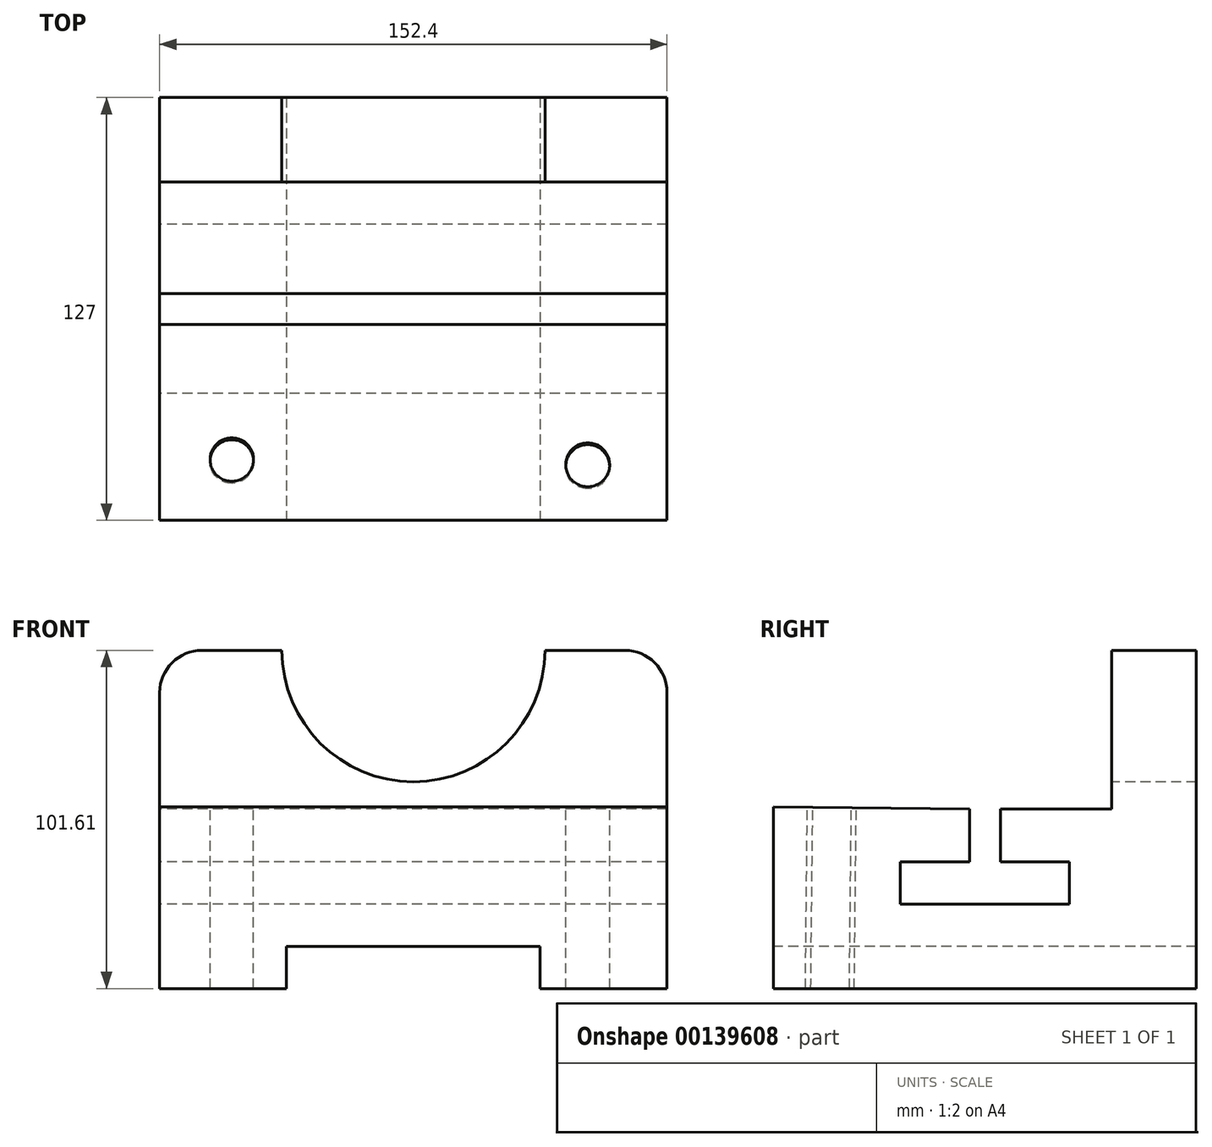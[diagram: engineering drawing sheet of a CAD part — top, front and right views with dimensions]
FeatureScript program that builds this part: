
annotation { "Feature Type Name" : "Feature", "Feature Type Description" : "" }
export const myFeature = defineFeature(function(context is Context, id is Id, definition is map)
    precondition{}
    {
        {
            var Q0;
            Q0=qCreatedBy(makeId("Right.planeOp"),FACE);
            var sketch = newSketch(context, id + "F0", { "sketchPlane" : qUnion([Q0])});
            skLineSegment(sketch, "E0", {"start": v(42.75, 47.63) * mm, "end": v(42.75, 0) * mm});
            skLineSegment(sketch, "E1", {"start": v(42.75, 0) * mm, "end": v(9.3, 0) * mm});
            skLineSegment(sketch, "E2", {"start": v(9.3, 0) * mm, "end": v(9.3, -15.87) * mm});
            skLineSegment(sketch, "E3", {"start": v(9.3, -15.87) * mm, "end": v(30.05, -15.87) * mm});
            skLineSegment(sketch, "E4", {"start": v(30.05, -15.87) * mm, "end": v(30.05, -28.57) * mm});
            skLineSegment(sketch, "E5", {"start": v(30.05, -28.57) * mm, "end": v(-20.75, -28.58) * mm});
            skLineSegment(sketch, "E6", {"start": v(-20.75, -28.58) * mm, "end": v(-20.75, -15.88) * mm});
            skLineSegment(sketch, "E7", {"start": v(-20.75, -15.88) * mm, "end": v(0, -15.88) * mm});
            skLineSegment(sketch, "E8", {"start": v(0, -15.88) * mm, "end": v(0, 0) * mm});
            skLineSegment(sketch, "E9", {"start": v(42.75, 47.63) * mm, "end": v(68.15, 47.63) * mm});
            skLineSegment(sketch, "E10", {"start": v(68.15, 47.63) * mm, "end": v(68.15, -53.97) * mm});
            skLineSegment(sketch, "E11", {"start": v(68.15, -53.97) * mm, "end": v(-58.85, -53.98) * mm});
            skLineSegment(sketch, "E12", {"start": v(-58.85, -53.98) * mm, "end": v(-58.85, 0.64) * mm});
            skLineSegment(sketch, "E13", {"start": v(-58.85, 0.64) * mm, "end": v(0, 0) * mm});
            skSolve(sketch);
        }
        {
            var Q0;
            Q0 = qSketchRegion(id + "F0", true);
            extrude(context, id + "F1", {"entities" : qUnion([Q0]), "depth" : 152.4 * mm});
        }
        {
            var Q0;
            Q0=makeQuery(id+"F1.opExtrude","SWEPT_FACE",FACE,{"disambiguationData":[OSD([sQuery(id+"F0.wireOp",EDGE,"E12")])]});
            var sketch = newSketch(context, id + "F2", { "sketchPlane" : qUnion([Q0])});
            skLineSegment(sketch, "E14", {"start": v(38.1, -53.98) * mm, "end": v(38.1, -41.27) * mm});
            skLineSegment(sketch, "E15", {"start": v(38.1, -41.27) * mm, "end": v(114.3, -41.27) * mm});
            skLineSegment(sketch, "E16", {"start": v(114.3, -41.27) * mm, "end": v(114.3, -53.98) * mm});
            skSolve(sketch);
        }
        {
            var Q0;
            {var subQ0=sQuery(id+"F2.wireOp",EDGE,"E14");Q0=makeQuery(id+"F2.imprint","IMPRINT",FACE,{"disambiguationData":[TD([[makeQuery(id+"F2.imprint","IMPRINT",EDGE,{"derivedFrom":subQ0}),-1.0]])]});}
            extrude(context, id + "F3", {"entities" : qUnion([Q0]), "operationType" : NewBodyOperationType.REMOVE, "endBound" : BoundingType.THROUGH_ALL, "oppositeDirection" : true, "depth" : 127 * mm});
        }
        {
            var Q0;
            Q0=makeQuery(id+"F1.opExtrude","SWEPT_FACE",FACE,{"disambiguationData":[OSD([sQuery(id+"F0.wireOp",EDGE,"E0")])]});
            var sketch = newSketch(context, id + "F4", { "sketchPlane" : qUnion([Q0])});
            skCircle(sketch, "E17", {"center": v(76.2, 47.62) * mm, "radius": 39.5 * mm});
            skSolve(sketch);
        }
        {
            var Q0;
            Q0 = qSketchRegion(id + "F4", true);
            var Q1;
            {var subQ0=sQuery(id+"F4.wireOp",EDGE,"E17");var subQ1=makeQuery(id+"F1.opExtrude","SWEPT_EDGE",EDGE,{"disambiguationData":[OSD([sQuery(id+"F0.wireOp",EDGE,"E0"),sQuery(id+"F0.wireOp",EDGE,"E9")])]});var subQ2=makeQuery(id+"F4.imprint","INTERSECT",VERTEX,{"disambiguationData":[OD(0.0)],"derivedFrom":[subQ1,subQ0]});Q1=makeQuery(id+"F4.imprint","IMPRINT",FACE,{"disambiguationData":[TD([[makeQuery(id+"F4.imprint","IMPRINT",EDGE,{"disambiguationData":[TD([[subQ2,-1.0]])],"derivedFrom":subQ0}),1.0]])]});}
            extrude(context, id + "F5", {"entities" : qUnion([Q0, Q1]), "operationType" : NewBodyOperationType.REMOVE, "oppositeDirection" : true, "depth" : 25.4 * mm});
        }
        {
            var Q0;
            Q0=makeQuery(id+"F1.opExtrude","CAP_EDGE",EDGE,{"disambiguationData":[OSD([sQuery(id+"F0.wireOp",EDGE,"E9")])],"isStart":false});
            var Q1;
            Q1=makeQuery(id+"F1.opExtrude","CAP_EDGE",EDGE,{"disambiguationData":[OSD([sQuery(id+"F0.wireOp",EDGE,"E9")])],"isStart":true});
            fillet(context, id + "F6", {"entities" : qUnion([Q0, Q1]), "radius" : 12.7 * mm, "tangentPropagation" : true, "allowEdgeOverflow" : false});
        }
        {
            var Q0;
            Q0=makeQuery(id+"F1.opExtrude","SWEPT_FACE",FACE,{"disambiguationData":[OSD([sQuery(id+"F0.wireOp",EDGE,"E13")])]});
            var sketch = newSketch(context, id + "F7", { "sketchPlane" : qUnion([Q0])});
            skCircle(sketch, "E18", {"center": v(21.65, -40.56) * mm, "radius": 6.54 * mm});
            skCircle(sketch, "E19", {"center": v(128.56, -42.12) * mm, "radius": 6.6 * mm});
            skSolve(sketch);
        }
        {
            var Q0;
            Q0=makeQuery(id+"F7.imprint","IMPRINT",FACE,{"disambiguationData":[TD([[makeQuery(id+"F7.imprint","IMPRINT",EDGE,{"derivedFrom":sQuery(id+"F7.wireOp",EDGE,"E19")}),1.0]])]});
            var Q1;
            Q1=makeQuery(id+"F7.imprint","IMPRINT",FACE,{"disambiguationData":[TD([[makeQuery(id+"F7.imprint","IMPRINT",EDGE,{"derivedFrom":sQuery(id+"F7.wireOp",EDGE,"E18")}),1.0]])]});
            extrude(context, id + "F8", {"entities" : qUnion([Q0, Q1]), "operationType" : NewBodyOperationType.REMOVE, "endBound" : BoundingType.THROUGH_ALL, "oppositeDirection" : true, "depth" : 50.8 * mm});
        }
    });
